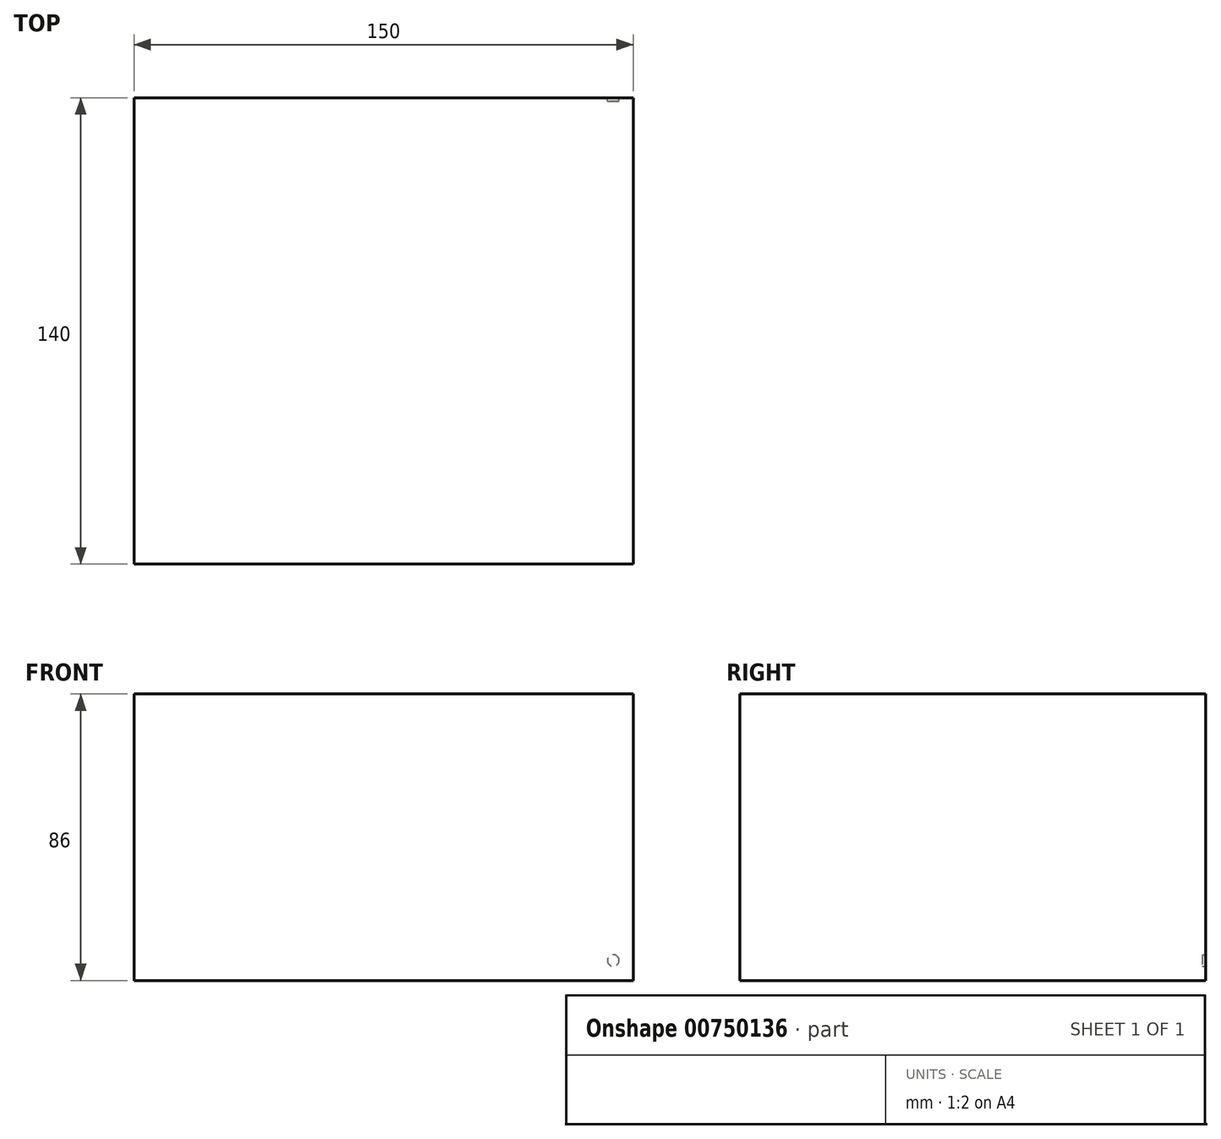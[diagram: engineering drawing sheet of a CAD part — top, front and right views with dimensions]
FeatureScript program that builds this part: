
annotation { "Feature Type Name" : "Feature", "Feature Type Description" : "" }
export const myFeature = defineFeature(function(context is Context, id is Id, definition is map)
    precondition{}
    {
        {
            var Q0;
            Q0=qCreatedBy(makeId("Front.planeOp"),FACE);
            var sketch = newSketch(context, id + "F0", { "sketchPlane" : qUnion([Q0])});
            skLineSegment(sketch, "E0.bottom", {"start": v(-75, 43) * mm, "end": v(75, 43) * mm});
            skLineSegment(sketch, "E0.top", {"start": v(-75, -43) * mm, "end": v(75, -43) * mm});
            skLineSegment(sketch, "E0.left", {"start": v(-75, 43) * mm, "end": v(-75, -43) * mm});
            skLineSegment(sketch, "E0.right", {"start": v(75, 43) * mm, "end": v(75, -43) * mm});
            skPoint(sketch, "E0.middle", {"position": v(0, 0) * mm});
            skSolve(sketch);
        }
        {
            var Q0;
            Q0=makeQuery(id+"F0.imprint","IMPRINT",FACE,{"disambiguationData":[TD([[makeQuery(id+"F0.imprint","IMPRINT",EDGE,{"derivedFrom":sQuery(id+"F0.wireOp",EDGE,"E0.bottom")}),-1.0]])]});
            extrude(context, id + "F1", {"entities" : qUnion([Q0]), "depth" : 140 * mm, "offsetDistance" : 25 * mm});
        }
        {
            var Q0;
            Q0=makeQuery(id+"F1.opExtrude","CAP_FACE",FACE,{"disambiguationData":[OSD([sQuery(id+"F0.wireOp",EDGE,"E0.bottom"),sQuery(id+"F0.wireOp",EDGE,"E0.top"),sQuery(id+"F0.wireOp",EDGE,"E0.left"),sQuery(id+"F0.wireOp",EDGE,"E0.right")])],"isStart":true});
            var sketch = newSketch(context, id + "F2", { "sketchPlane" : qUnion([Q0])});
            skCircle(sketch, "E1", {"center": v(-69, -37) * mm, "radius": 1.75 * mm});
            skSolve(sketch);
        }
        {
            var Q0;
            Q0=makeQuery(id+"F2.imprint","IMPRINT",FACE,{"disambiguationData":[TD([[makeQuery(id+"F2.imprint","IMPRINT",EDGE,{"derivedFrom":sQuery(id+"F2.wireOp",EDGE,"E1")}),1.0]])]});
            extrude(context, id + "F3", {"entities" : qUnion([Q0]), "operationType" : NewBodyOperationType.REMOVE, "oppositeDirection" : true, "depth" : 1 * mm, "offsetDistance" : 25 * mm});
        }
    });
